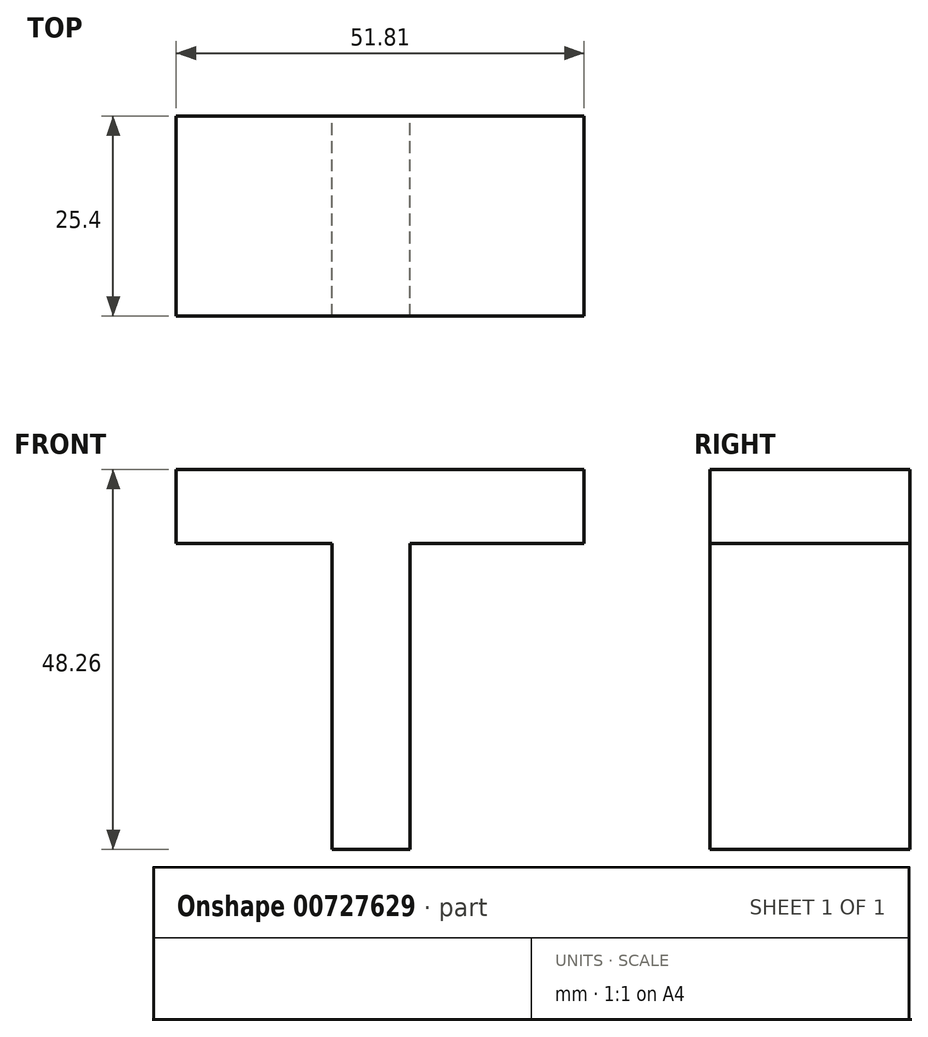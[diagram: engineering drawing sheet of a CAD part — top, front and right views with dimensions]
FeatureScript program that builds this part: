
annotation { "Feature Type Name" : "Feature", "Feature Type Description" : "" }
export const myFeature = defineFeature(function(context is Context, id is Id, definition is map)
    precondition{}
    {
        {
            var Q0;
            Q0=qCreatedBy(makeId("Front.planeOp"),FACE);
            var sketch = newSketch(context, id + "F0", { "sketchPlane" : qUnion([Q0])});
            skLineSegment(sketch, "E0.bottom", {"start": v(-12.38, -26.6) * mm, "end": v(-2.48, -26.6) * mm});
            skLineSegment(sketch, "E0.top", {"start": v(-12.38, 12.26) * mm, "end": v(-2.48, 12.26) * mm});
            skLineSegment(sketch, "E0.left", {"start": v(-12.38, -26.6) * mm, "end": v(-12.38, 12.26) * mm});
            skLineSegment(sketch, "E0.right", {"start": v(-2.48, -26.6) * mm, "end": v(-2.48, 12.26) * mm});
            skPoint(sketch, "E1.oppositeSnap0", {"position": v(-7.43, 12.26) * mm});
            skLineSegment(sketch, "E1.bottom", {"start": v(-32.2, 21.65) * mm, "end": v(19.62, 21.65) * mm});
            skLineSegment(sketch, "E1.top", {"start": v(-32.2, 12.26) * mm, "end": v(19.62, 12.26) * mm});
            skLineSegment(sketch, "E1.left", {"start": v(-32.2, 21.65) * mm, "end": v(-32.2, 12.26) * mm});
            skLineSegment(sketch, "E1.right", {"start": v(19.62, 21.65) * mm, "end": v(19.62, 12.26) * mm});
            skSolve(sketch);
        }
        {
            var Q0;
            Q0=makeQuery(id+"F0.imprint","IMPRINT",FACE,{"disambiguationData":[TD([[makeQuery(id+"F0.imprint","IMPRINT",EDGE,{"derivedFrom":sQuery(id+"F0.wireOp",EDGE,"E0.bottom")}),1.0]])]});
            var Q1;
            Q1=makeQuery(id+"F0.imprint","IMPRINT",FACE,{"disambiguationData":[TD([[makeQuery(id+"F0.imprint","IMPRINT",EDGE,{"derivedFrom":sQuery(id+"F0.wireOp",EDGE,"E1.bottom")}),-1.0]])]});
            extrude(context, id + "F1", {"entities" : qUnion([Q0, Q1]), "depth" : 25.4 * mm, "offsetDistance" : 25.4 * mm});
        }
    });
